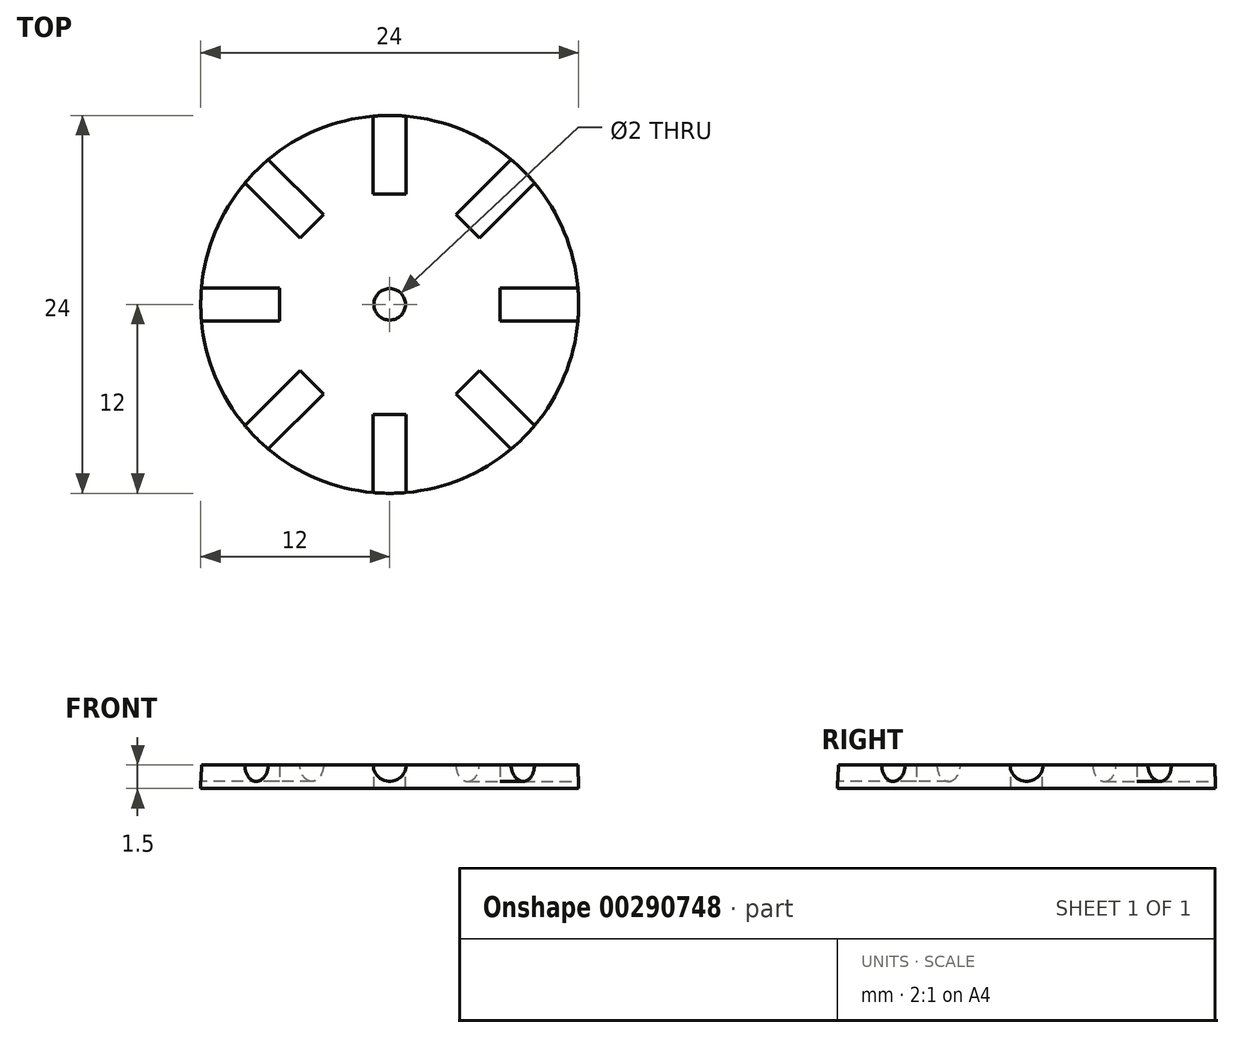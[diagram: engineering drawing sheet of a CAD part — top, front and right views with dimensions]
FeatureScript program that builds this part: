
annotation { "Feature Type Name" : "Feature", "Feature Type Description" : "" }
export const myFeature = defineFeature(function(context is Context, id is Id, definition is map)
    precondition{}
    {
        {
            var Q0;
            Q0=qCreatedBy(makeId("Top.planeOp"),FACE);
            var sketch = newSketch(context, id + "F0", { "sketchPlane" : qUnion([Q0])});
            skCircle(sketch, "E0", {"center": v(0, 0) * mm, "radius": 12 * mm});
            skSolve(sketch);
        }
        {
            var Q0;
            Q0 = qSketchRegion(id + "F0", true);
            extrude(context, id + "F1", {"entities" : qUnion([Q0]), "depth" : 1.5 * mm});
        }
        {
            var Q0;
            Q0=qCreatedBy(makeId("Front.planeOp"),FACE);
            cPlane(context, id + "F2", {"entities" : qUnion([Q0]), "cplaneType" : CPlaneType.OFFSET, "offset" : 12 * mm, "width" : 150 * mm, "height" : 150 * mm});
        }
        {
            var Q0;
            Q0=qCreatedBy(id+"F2.planeOp",FACE);
            var sketch = newSketch(context, id + "F3", { "sketchPlane" : qUnion([Q0])});
            skCircle(sketch, "E1", {"center": v(0, 1.5) * mm, "radius": 1.05 * mm});
            skSolve(sketch);
        }
        {
            var Q0;
            Q0=makeQuery(id+"F3.imprint","IMPRINT",FACE,{"disambiguationData":[TD([[makeQuery(id+"F3.imprint","IMPRINT",EDGE,{"derivedFrom":sQuery(id+"F3.wireOp",EDGE,"E1")}),1.0]])]});
            extrude(context, id + "F4", {"entities" : qUnion([Q0]), "oppositeDirection" : true, "depth" : 5 * mm});
        }
        {
            var Q0;
            Q0=qCreatedBy(makeId("Right.planeOp"),FACE);
            var sketch = newSketch(context, id + "F5", { "sketchPlane" : qUnion([Q0])});
            skLineSegment(sketch, "E2", {"start": v(0, -9.01) * mm, "end": v(0, 11.79) * mm});
            skSolve(sketch);
        }
        {
            var Q0;
            Q0=makeQuery(id+"F4.opExtrude","SWEPT_BODY",BODY,{"disambiguationData":[OSD([sQuery(id+"F3.wireOp",EDGE,"E1")])]});
            var Q1;
            Q1=sQuery(id+"F5.wireOp",EDGE,"E2");
            circularPattern(context, id + "F6", {"operationType" : NewBodyOperationType.REMOVE, "entities" : qUnion([Q0]), "axis" : qUnion([Q1]), "angle" : 360 * degree, "instanceCount" : 8, "equalSpace" : true});
        }
        {
            var Q0;
            Q0=makeQuery(id+"F1.opExtrude","CAP_FACE",FACE,{"disambiguationData":[OSD([sQuery(id+"F0.wireOp",EDGE,"E0")])],"isStart":false});
            var sketch = newSketch(context, id + "F7", { "sketchPlane" : qUnion([Q0])});
            skCircle(sketch, "E3", {"center": v(0, 0) * mm, "radius": 1 * mm});
            skSolve(sketch);
        }
        {
            var Q0;
            Q0 = qSketchRegion(id + "F7", true);
            extrude(context, id + "F8", {"entities" : qUnion([Q0]), "operationType" : NewBodyOperationType.REMOVE, "endBound" : BoundingType.UP_TO_NEXT, "oppositeDirection" : true, "depth" : 25 * mm});
        }
    });
